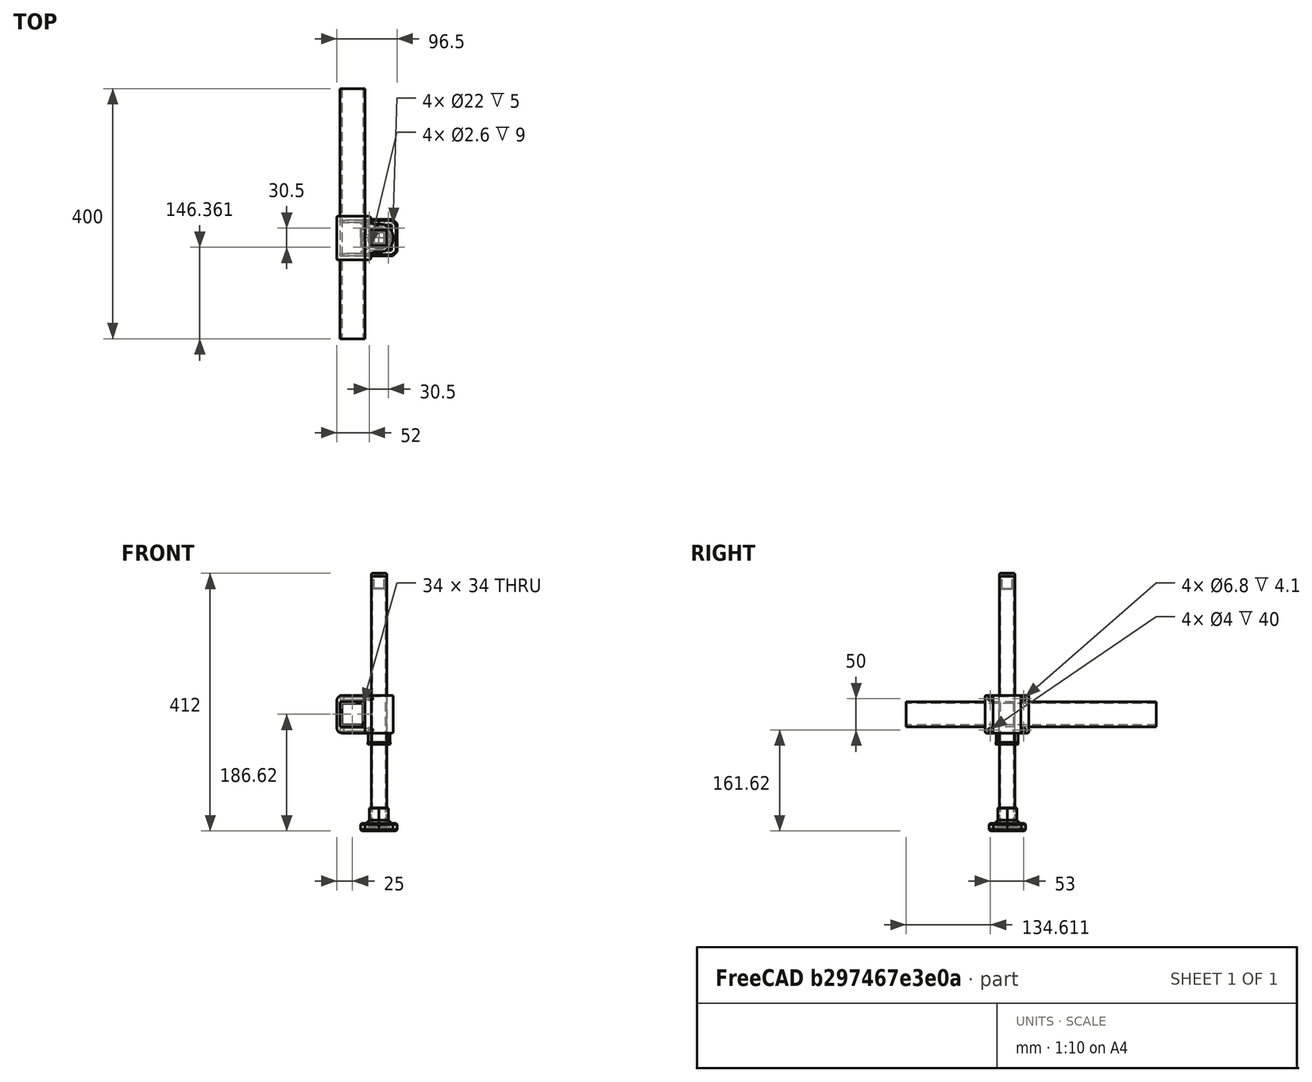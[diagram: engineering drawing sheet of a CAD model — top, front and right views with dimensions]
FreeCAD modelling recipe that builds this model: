
FCSTD DOCUMENT  (FreeCAD 0.21R33771 (Git))
Label: BG_DaichselStütze 2.0
License: All rights reserved
LicenseURL: http://en.wikipedia.org/wiki/All_rights_reserved
objects: App::FeaturePython×32, Part::FeaturePython×10
note: 10 computed .brp shape members not serialized (recipe doc carries the construction recipe); baked Part::Feature solids carry a one-line shape summary decoded from their .brp

FEATURE [Part::FeaturePython] b_DeichselRohr_001_  label="DeichselRohr_001"  # a2plus imported part (geometry in sourceFile) (typed FeaturePython)
  Placement = pos=(0,11,0) rot=(0,0,1;0rad)
  a2p_Version = 0.4.60n
  fixedPosition = true
  objectType = a2pPart
  sourceFile = ./../DeichselRohr/DeichselRohr.FCStd
  subassemblyImport = false
  timeLastImport = 1.69101e+09
  updateColors = true
FEATURE [Part::FeaturePython] b_DeichselSchelle_2_0_001_  label="DeichselSchelle 2.0_001"  # a2plus imported part (geometry in sourceFile) (typed FeaturePython)
  Placement = pos=(20,-192.889,1.11766e-08) rot=(0,0,1;0rad)
  a2p_Version = 0.4.60n
  fixedPosition = false
  objectType = a2pPart
  sourceFile = ./../DaichselSchelle 2.0/DeichselSchelle 2.0.FCStd
  subassemblyImport = false
  timeLastImport = 1.69119e+09
  updateColors = true
FEATURE [Part::FeaturePython] b_Deichselst_xc3_xbctze_2_0_St_xc3_xbctzenklemme_001_  label="Deichselstütze 2.0 Stützenklemme_001"  # a2plus imported part (geometry in sourceFile) (typed FeaturePython)
  Placement = pos=(42.75,-227.889,-30) rot=(0,0,1;0rad)
  a2p_Version = 0.4.60n
  fixedPosition = false
  objectType = a2pPart
  sourceFile = ./../Deichselstütze 2.0 Stützenklemme/Deichselstütze 2.0 Stützenklemme.FCStd
  subassemblyImport = false
  timeLastImport = 1.69119e+09
  updateColors = true
FEATURE [Part::FeaturePython] Screw  label="M4x40-Screw"  # Fasteners workbench fastener (typed FeaturePython)
  Placement = pos=(25.9,-254.389,25) rot=(0,1,0;1.5708rad)
  diameter = 5
  invert = false
  leftHanded = false
  length = 10
  lengthCustom = 40
  matchOuter = false
  offset = 0
  thread = false
  type = 45
FEATURE [Part::FeaturePython] Screw001  label="M4x40-Screw018"  # Fasteners workbench fastener (typed FeaturePython)
  Placement = pos=(25.9,-201.389,25) rot=(-0.545713,0.63592,-0.545713;2.00877rad)
  diameter = 5
  invert = false
  leftHanded = false
  length = 10
  lengthCustom = 40
  matchOuter = false
  offset = 0
  thread = false
  type = 45
FEATURE [Part::FeaturePython] Screw002  label="M4x40-Screw019"  # Fasteners workbench fastener (typed FeaturePython)
  Placement = pos=(25.9,-254.389,-25) rot=(0.579547,-0.572931,0.579547;4.18215rad)
  diameter = 5
  invert = false
  leftHanded = false
  length = 10
  lengthCustom = 40
  matchOuter = false
  offset = 0
  thread = false
  type = 45
FEATURE [Part::FeaturePython] Screw003  label="M4x40-Screw020"  # Fasteners workbench fastener (typed FeaturePython)
  Placement = pos=(25.9,-201.389,-25) rot=(0.684336,0.251731,0.684336;2.64838rad)
  diameter = 5
  invert = false
  leftHanded = false
  length = 10
  lengthCustom = 40
  matchOuter = false
  offset = 0
  thread = false
  type = 45
FEATURE [App::FeaturePython] axisCoincident_001  label="axisCoincident_001__DeichselSchelle 2.0_001"  # a2plus constraint (typed FeaturePython)
  Object1 = b_DeichselRohr_001_
  Object2 = b_DeichselSchelle_2_0_001_
  ParentTreeObject = -> b_DeichselRohr_001_
  SubElement1 = Edge8
  SubElement2 = Edge16
  Suppressed = false
  Type = axial
  directionConstraint = 0
  lockRotation = false
FEATURE [App::FeaturePython] axisCoincident_001_mirror  label="axisCoincident_001__DeichselRohr_001"  # a2plus constraint (typed FeaturePython)
  Object1 = b_DeichselRohr_001_
  Object2 = b_DeichselSchelle_2_0_001_
  ParentTreeObject = -> b_DeichselSchelle_2_0_001_
  SubElement1 = Edge8
  SubElement2 = Edge16
  Suppressed = false
  Type = axial
  directionConstraint = 0
  lockRotation = false
FEATURE [App::FeaturePython] axisCoincident_002  label="axisCoincident_002__DeichselSchelle 2.0_001"  # a2plus constraint (typed FeaturePython)
  Object1 = Screw
  Object2 = b_DeichselSchelle_2_0_001_
  ParentTreeObject = -> Screw
  SubElement1 = Face17
  SubElement2 = Face12
  Suppressed = false
  Type = axial
  directionConstraint = 1
  lockRotation = false
FEATURE [App::FeaturePython] axisCoincident_002_mirror  label="axisCoincident_002__M4x40-Screw"  # a2plus constraint (typed FeaturePython)
  Object1 = Screw
  Object2 = b_DeichselSchelle_2_0_001_
  ParentTreeObject = -> b_DeichselSchelle_2_0_001_
  SubElement1 = Face17
  SubElement2 = Face12
  Suppressed = false
  Type = axial
  directionConstraint = 1
  lockRotation = false
FEATURE [App::FeaturePython] axisCoincident_003  label="axisCoincident_003__DeichselSchelle 2.0_001"  # a2plus constraint (typed FeaturePython)
  Object1 = Screw001
  Object2 = b_DeichselSchelle_2_0_001_
  ParentTreeObject = -> Screw001
  SubElement1 = Face17
  SubElement2 = Face13
  Suppressed = false
  Type = axial
  directionConstraint = 1
  lockRotation = false
FEATURE [App::FeaturePython] axisCoincident_003_mirror  label="axisCoincident_003__M4x40-Screw001"  # a2plus constraint (typed FeaturePython)
  Object1 = Screw001
  Object2 = b_DeichselSchelle_2_0_001_
  ParentTreeObject = -> b_DeichselSchelle_2_0_001_
  SubElement1 = Face17
  SubElement2 = Face13
  Suppressed = false
  Type = axial
  directionConstraint = 1
  lockRotation = false
FEATURE [App::FeaturePython] axisCoincident_004  label="axisCoincident_004__DeichselSchelle 2.0_001"  # a2plus constraint (typed FeaturePython)
  Object1 = Screw002
  Object2 = b_DeichselSchelle_2_0_001_
  ParentTreeObject = -> Screw002
  SubElement1 = Face17
  SubElement2 = Face27
  Suppressed = false
  Type = axial
  directionConstraint = 1
  lockRotation = false
FEATURE [App::FeaturePython] axisCoincident_004_mirror  label="axisCoincident_004__M4x40-Screw002"  # a2plus constraint (typed FeaturePython)
  Object1 = Screw002
  Object2 = b_DeichselSchelle_2_0_001_
  ParentTreeObject = -> b_DeichselSchelle_2_0_001_
  SubElement1 = Face17
  SubElement2 = Face27
  Suppressed = false
  Type = axial
  directionConstraint = 1
  lockRotation = false
FEATURE [App::FeaturePython] axisCoincident_005  label="axisCoincident_005__DeichselSchelle 2.0_001"  # a2plus constraint (typed FeaturePython)
  Object1 = Screw003
  Object2 = b_DeichselSchelle_2_0_001_
  ParentTreeObject = -> Screw003
  SubElement1 = Face17
  SubElement2 = Face28
  Suppressed = false
  Type = axial
  directionConstraint = 1
  lockRotation = false
FEATURE [App::FeaturePython] axisCoincident_005_mirror  label="axisCoincident_005__M4x40-Screw003"  # a2plus constraint (typed FeaturePython)
  Object1 = Screw003
  Object2 = b_DeichselSchelle_2_0_001_
  ParentTreeObject = -> b_DeichselSchelle_2_0_001_
  SubElement1 = Face17
  SubElement2 = Face28
  Suppressed = false
  Type = axial
  directionConstraint = 1
  lockRotation = false
FEATURE [App::FeaturePython] planeCoincident_001  label="planeCoincident_001__Deichselstütze 2.0 Stützenklemme_001"  # a2plus constraint (typed FeaturePython)
  Object1 = Screw
  Object2 = b_Deichselst_xc3_xbctze_2_0_St_xc3_xbctzenklemme_001_
  ParentTreeObject = -> Screw
  SubElement1 = Face13
  SubElement2 = Face82
  Suppressed = false
  Type = plane
  directionConstraint = 0
  offset = 0
FEATURE [App::FeaturePython] planeCoincident_001_mirror  label="planeCoincident_001__M4x40-Screw"  # a2plus constraint (typed FeaturePython)
  Object1 = Screw
  Object2 = b_Deichselst_xc3_xbctze_2_0_St_xc3_xbctzenklemme_001_
  ParentTreeObject = -> b_Deichselst_xc3_xbctze_2_0_St_xc3_xbctzenklemme_001_
  SubElement1 = Face13
  SubElement2 = Face82
  Suppressed = false
  Type = plane
  directionConstraint = 0
  offset = 0
FEATURE [App::FeaturePython] planeCoincident_002  label="planeCoincident_002__DeichselSchelle 2.0_001"  # a2plus constraint (typed FeaturePython)
  Object1 = b_Deichselst_xc3_xbctze_2_0_St_xc3_xbctzenklemme_001_
  Object2 = b_DeichselSchelle_2_0_001_
  ParentTreeObject = -> b_Deichselst_xc3_xbctze_2_0_St_xc3_xbctzenklemme_001_
  SubElement1 = Face6
  SubElement2 = Face5
  Suppressed = false
  Type = plane
  directionConstraint = 1
  offset = 0
FEATURE [App::FeaturePython] planeCoincident_002_mirror  label="planeCoincident_002__Deichselstütze 2.0 Stützenklemme_001"  # a2plus constraint (typed FeaturePython)
  Object1 = b_Deichselst_xc3_xbctze_2_0_St_xc3_xbctzenklemme_001_
  Object2 = b_DeichselSchelle_2_0_001_
  ParentTreeObject = -> b_DeichselSchelle_2_0_001_
  SubElement1 = Face6
  SubElement2 = Face5
  Suppressed = false
  Type = plane
  directionConstraint = 1
  offset = 0
FEATURE [App::FeaturePython] planeCoincident_003  label="planeCoincident_003__Deichselstütze 2.0 Stützenklemme_001"  # a2plus constraint (typed FeaturePython)
  Object1 = Screw002
  Object2 = b_Deichselst_xc3_xbctze_2_0_St_xc3_xbctzenklemme_001_
  ParentTreeObject = -> Screw002
  SubElement1 = Face13
  SubElement2 = Face80
  Suppressed = false
  Type = plane
  directionConstraint = 0
  offset = 0
FEATURE [App::FeaturePython] planeCoincident_003_mirror  label="planeCoincident_003__M4x40-Screw014"  # a2plus constraint (typed FeaturePython)
  Object1 = Screw002
  Object2 = b_Deichselst_xc3_xbctze_2_0_St_xc3_xbctzenklemme_001_
  ParentTreeObject = -> b_Deichselst_xc3_xbctze_2_0_St_xc3_xbctzenklemme_001_
  SubElement1 = Face13
  SubElement2 = Face80
  Suppressed = false
  Type = plane
  directionConstraint = 0
  offset = 0
FEATURE [App::FeaturePython] planeCoincident_004  label="planeCoincident_004__M4x40-Screw011"  # a2plus constraint (typed FeaturePython)
  Object1 = b_Deichselst_xc3_xbctze_2_0_St_xc3_xbctzenklemme_001_
  Object2 = Screw001
  ParentTreeObject = -> b_Deichselst_xc3_xbctze_2_0_St_xc3_xbctzenklemme_001_
  SubElement1 = Face81
  SubElement2 = Face13
  Suppressed = false
  Type = plane
  directionConstraint = 0
  offset = 0
FEATURE [App::FeaturePython] planeCoincident_004_mirror  label="planeCoincident_004__Deichselstütze 2.0 Stützenklemme_001"  # a2plus constraint (typed FeaturePython)
  Object1 = b_Deichselst_xc3_xbctze_2_0_St_xc3_xbctzenklemme_001_
  Object2 = Screw001
  ParentTreeObject = -> Screw001
  SubElement1 = Face81
  SubElement2 = Face13
  Suppressed = false
  Type = plane
  directionConstraint = 0
  offset = 0
FEATURE [App::FeaturePython] planeCoincident_005  label="planeCoincident_005__Deichselstütze 2.0 Stützenklemme_001"  # a2plus constraint (typed FeaturePython)
  Object1 = Screw003
  Object2 = b_Deichselst_xc3_xbctze_2_0_St_xc3_xbctzenklemme_001_
  ParentTreeObject = -> Screw003
  SubElement1 = Face13
  SubElement2 = Face79
  Suppressed = false
  Type = plane
  directionConstraint = 0
  offset = 0
FEATURE [App::FeaturePython] planeCoincident_005_mirror  label="planeCoincident_005__M4x40-Screw013"  # a2plus constraint (typed FeaturePython)
  Object1 = Screw003
  Object2 = b_Deichselst_xc3_xbctze_2_0_St_xc3_xbctzenklemme_001_
  ParentTreeObject = -> b_Deichselst_xc3_xbctze_2_0_St_xc3_xbctzenklemme_001_
  SubElement1 = Face13
  SubElement2 = Face79
  Suppressed = false
  Type = plane
  directionConstraint = 0
  offset = 0
FEATURE [Part::FeaturePython] b_Deichselst_xc3_xbctzeFu_xc3_x9f_001_  label="DeichselstützeFuß_001"  # a2plus imported part (geometry in sourceFile) (typed FeaturePython)
  Placement = pos=(42.25,-227.389,-186.624) rot=(0,0,1;0rad)
  a2p_Version = 0.4.60n
  fixedPosition = false
  objectType = a2pPart
  sourceFile = ./../DeichselstützeFuß/DeichselstützeFuß.FCStd
  subassemblyImport = false
  timeLastImport = 1.72002e+09
  updateColors = true
FEATURE [Part::FeaturePython] b_Kappe_St_xc3_xbctze_001_  label="Kappe Stütze_001"  # a2plus imported part (geometry in sourceFile) (typed FeaturePython)
  Placement = pos=(55,-240.139,225.376) rot=(0,1,0;3.14159rad)
  a2p_Version = 0.4.60n
  fixedPosition = false
  objectType = a2pPart
  sourceFile = ./../DeichselstützeKappe/Kappe Stütze.FCStd
  subassemblyImport = false
  timeLastImport = 1685283389
  updateColors = true
FEATURE [Part::FeaturePython] b_AluVierkantRohr_400mm_001_  label="AluVierkantRohr 400mm_001"  # a2plus imported part (geometry in sourceFile) (typed FeaturePython)
  Placement = pos=(55,-240.139,-179.624) rot=(0,0,1;0rad)
  a2p_Version = 0.4.60n
  fixedPosition = false
  objectType = a2pPart
  sourceFile = ./Stützenrohr/AluVierkantRohr 400mm.FCStd
  subassemblyImport = false
  timeLastImport = 1.72003e+09
  updateColors = true
FEATURE [App::FeaturePython] planeCoincident_006  label="planeCoincident_006__Deichselstütze 2.0 Stützenklemme_001"  # a2plus constraint (typed FeaturePython)
  Object1 = b_AluVierkantRohr_400mm_001_
  Object2 = b_Deichselst_xc3_xbctze_2_0_St_xc3_xbctzenklemme_001_
  ParentTreeObject = -> b_AluVierkantRohr_400mm_001_
  SubElement1 = Face2
  SubElement2 = Face26
  Suppressed = false
  Type = plane
  directionConstraint = 0
  offset = 0
FEATURE [App::FeaturePython] planeCoincident_006_mirror  label="planeCoincident_006__AluVierkantRohr 400mm_001"  # a2plus constraint (typed FeaturePython)
  Object1 = b_AluVierkantRohr_400mm_001_
  Object2 = b_Deichselst_xc3_xbctze_2_0_St_xc3_xbctzenklemme_001_
  ParentTreeObject = -> b_Deichselst_xc3_xbctze_2_0_St_xc3_xbctzenklemme_001_
  SubElement1 = Face2
  SubElement2 = Face26
  Suppressed = false
  Type = plane
  directionConstraint = 0
  offset = 0
FEATURE [App::FeaturePython] planeCoincident_007  label="planeCoincident_007__Deichselstütze 2.0 Stützenklemme_001"  # a2plus constraint (typed FeaturePython)
  Object1 = b_AluVierkantRohr_400mm_001_
  Object2 = b_Deichselst_xc3_xbctze_2_0_St_xc3_xbctzenklemme_001_
  ParentTreeObject = -> b_AluVierkantRohr_400mm_001_
  SubElement1 = Face3
  SubElement2 = Face28
  Suppressed = false
  Type = plane
  directionConstraint = 0
  offset = 0
FEATURE [App::FeaturePython] planeCoincident_007_mirror  label="planeCoincident_007__AluVierkantRohr 400mm_001"  # a2plus constraint (typed FeaturePython)
  Object1 = b_AluVierkantRohr_400mm_001_
  Object2 = b_Deichselst_xc3_xbctze_2_0_St_xc3_xbctzenklemme_001_
  ParentTreeObject = -> b_Deichselst_xc3_xbctze_2_0_St_xc3_xbctzenklemme_001_
  SubElement1 = Face3
  SubElement2 = Face28
  Suppressed = false
  Type = plane
  directionConstraint = 0
  offset = 0
FEATURE [App::FeaturePython] planeCoincident_008  label="planeCoincident_008__DeichselstützeFuß_001"  # a2plus constraint (typed FeaturePython)
  Object1 = b_AluVierkantRohr_400mm_001_
  Object2 = b_Deichselst_xc3_xbctzeFu_xc3_x9f_001_
  ParentTreeObject = -> b_AluVierkantRohr_400mm_001_
  SubElement1 = Face9
  SubElement2 = Face108
  Suppressed = false
  Type = plane
  directionConstraint = 0
  offset = 0
FEATURE [App::FeaturePython] planeCoincident_008_mirror  label="planeCoincident_008__AluVierkantRohr 400mm_001"  # a2plus constraint (typed FeaturePython)
  Object1 = b_AluVierkantRohr_400mm_001_
  Object2 = b_Deichselst_xc3_xbctzeFu_xc3_x9f_001_
  ParentTreeObject = -> b_Deichselst_xc3_xbctzeFu_xc3_x9f_001_
  SubElement1 = Face9
  SubElement2 = Face108
  Suppressed = false
  Type = plane
  directionConstraint = 0
  offset = 0
FEATURE [App::FeaturePython] axisCoincident_006  label="axisCoincident_006__DeichselstützeFuß_001"  # a2plus constraint (typed FeaturePython)
  Object1 = b_AluVierkantRohr_400mm_001_
  Object2 = b_Deichselst_xc3_xbctzeFu_xc3_x9f_001_
  ParentTreeObject = -> b_AluVierkantRohr_400mm_001_
  SubElement1 = Edge5
  SubElement2 = Edge61
  Suppressed = false
  Type = axial
  directionConstraint = 0
  lockRotation = false
FEATURE [App::FeaturePython] axisCoincident_006_mirror  label="axisCoincident_006__AluVierkantRohr 400mm_001"  # a2plus constraint (typed FeaturePython)
  Object1 = b_AluVierkantRohr_400mm_001_
  Object2 = b_Deichselst_xc3_xbctzeFu_xc3_x9f_001_
  ParentTreeObject = -> b_Deichselst_xc3_xbctzeFu_xc3_x9f_001_
  SubElement1 = Edge5
  SubElement2 = Edge61
  Suppressed = false
  Type = axial
  directionConstraint = 0
  lockRotation = false
FEATURE [App::FeaturePython] axisCoincident_007  label="axisCoincident_007__AluVierkantRohr 400mm_001"  # a2plus constraint (typed FeaturePython)
  Object1 = b_Kappe_St_xc3_xbctze_001_
  Object2 = b_AluVierkantRohr_400mm_001_
  ParentTreeObject = -> b_Kappe_St_xc3_xbctze_001_
  SubElement1 = Edge17
  SubElement2 = Edge10
  Suppressed = false
  Type = axial
  directionConstraint = 1
  lockRotation = false
FEATURE [App::FeaturePython] axisCoincident_007_mirror  label="axisCoincident_007__Kappe Stütze_001"  # a2plus constraint (typed FeaturePython)
  Object1 = b_Kappe_St_xc3_xbctze_001_
  Object2 = b_AluVierkantRohr_400mm_001_
  ParentTreeObject = -> b_AluVierkantRohr_400mm_001_
  SubElement1 = Edge17
  SubElement2 = Edge10
  Suppressed = false
  Type = axial
  directionConstraint = 1
  lockRotation = false
FEATURE [App::FeaturePython] planeCoincident_009  label="planeCoincident_009__AluVierkantRohr 400mm_001"  # a2plus constraint (typed FeaturePython)
  Object1 = b_Kappe_St_xc3_xbctze_001_
  Object2 = b_AluVierkantRohr_400mm_001_
  ParentTreeObject = -> b_Kappe_St_xc3_xbctze_001_
  SubElement1 = Face7
  SubElement2 = Face6
  Suppressed = false
  Type = plane
  directionConstraint = 1
  offset = 0
FEATURE [App::FeaturePython] planeCoincident_009_mirror  label="planeCoincident_009__Kappe Stütze_001"  # a2plus constraint (typed FeaturePython)
  Object1 = b_Kappe_St_xc3_xbctze_001_
  Object2 = b_AluVierkantRohr_400mm_001_
  ParentTreeObject = -> b_AluVierkantRohr_400mm_001_
  SubElement1 = Face7
  SubElement2 = Face6
  Suppressed = false
  Type = plane
  directionConstraint = 1
  offset = 0
